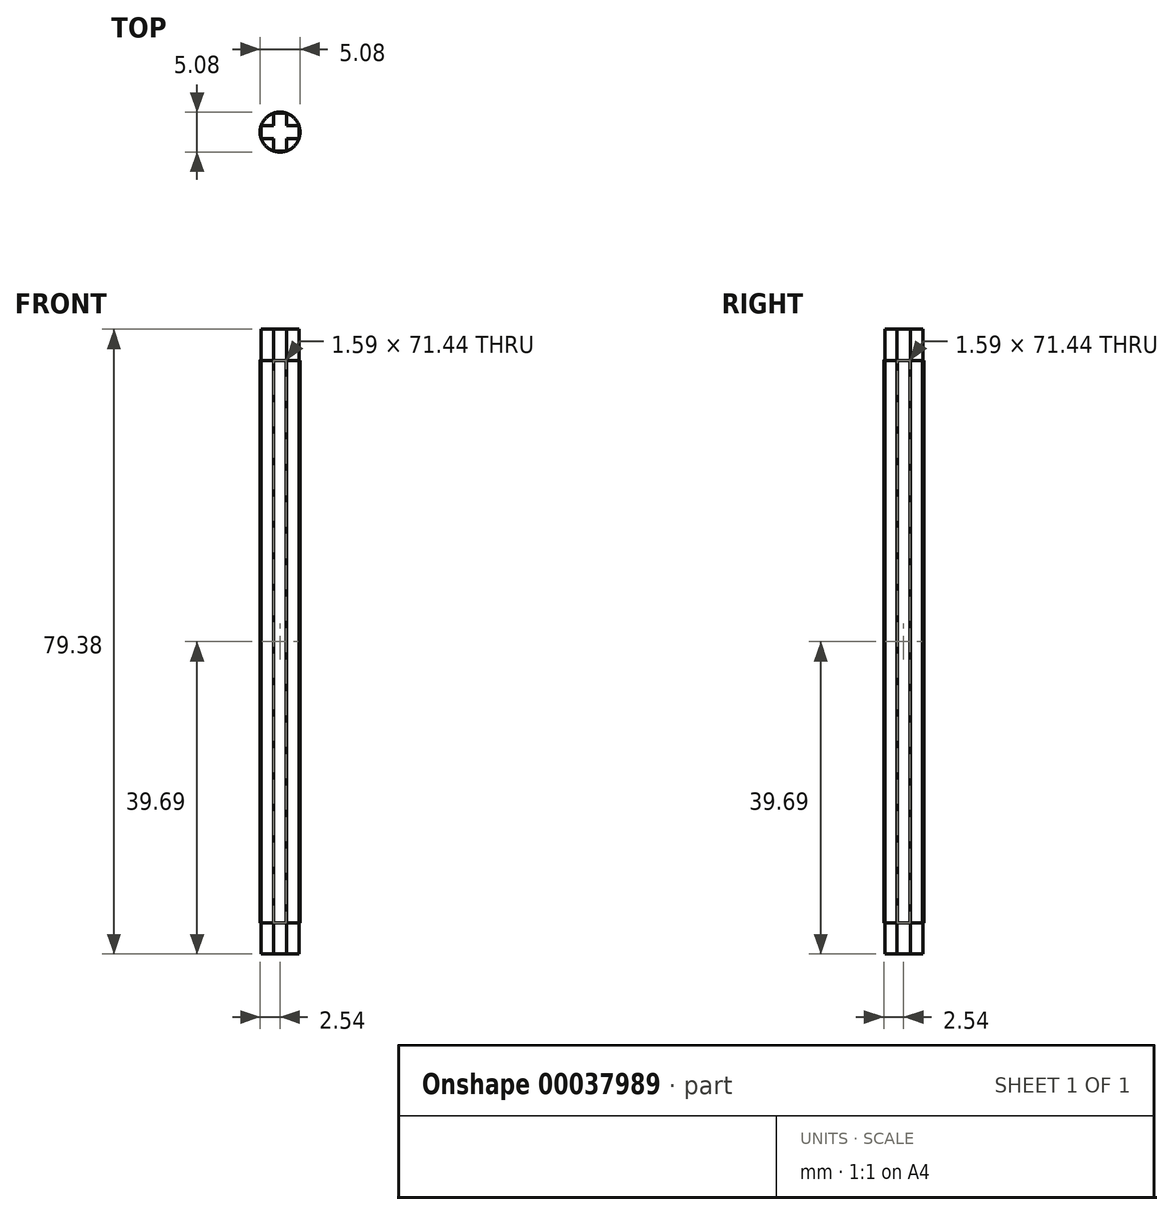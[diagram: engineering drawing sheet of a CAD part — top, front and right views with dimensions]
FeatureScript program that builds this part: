
annotation { "Feature Type Name" : "Feature", "Feature Type Description" : "" }
export const myFeature = defineFeature(function(context is Context, id is Id, definition is map)
    precondition{}
    {
        {
            var Q0;
            Q0=qCreatedBy(makeId("Top.planeOp"),FACE);
            var sketch = newSketch(context, id + "F0", { "sketchPlane" : qUnion([Q0])});
            skLineSegment(sketch, "E0.rect.bottom", {"start": v(0.84, -2.41) * mm, "end": v(-0.84, -2.41) * mm});
            skLineSegment(sketch, "E0.rect.top", {"start": v(0.84, 2.41) * mm, "end": v(-0.84, 2.41) * mm});
            skLineSegment(sketch, "E0.rect.left", {"start": v(0.84, -2.41) * mm, "end": v(0.84, 2.41) * mm});
            skLineSegment(sketch, "E0.rect.right", {"start": v(-0.84, -2.41) * mm, "end": v(-0.84, 2.41) * mm});
            skPoint(sketch, "E0.rect.middle", {"position": v(0, 0) * mm});
            skLineSegment(sketch, "E1.rect.bottom", {"start": v(2.41, -0.84) * mm, "end": v(-2.41, -0.84) * mm});
            skLineSegment(sketch, "E1.rect.top", {"start": v(2.41, 0.84) * mm, "end": v(-2.41, 0.84) * mm});
            skLineSegment(sketch, "E1.rect.left", {"start": v(2.41, -0.84) * mm, "end": v(2.41, 0.84) * mm});
            skLineSegment(sketch, "E1.rect.right", {"start": v(-2.41, -0.84) * mm, "end": v(-2.41, 0.84) * mm});
            skSolve(sketch);
        }
        {
            var Q0;
            Q0 = qSketchRegion(id + "F0", true);
            extrude(context, id + "F1", {"entities" : qUnion([Q0]), "endBound" : BoundingType.SYMMETRIC, "depth" : 79.38 * mm});
        }
        {
            var Q0;
            Q0=qCreatedBy(makeId("Top.planeOp"),FACE);
            var sketch = newSketch(context, id + "F2", { "sketchPlane" : qUnion([Q0])});
            skCircle(sketch, "E2", {"center": v(0, 0) * mm, "radius": 2.54 * mm});
            skSolve(sketch);
        }
        {
            var Q0;
            Q0 = qSketchRegion(id + "F2", true);
            extrude(context, id + "F3", {"entities" : qUnion([Q0]), "operationType" : NewBodyOperationType.ADD, "endBound" : BoundingType.SYMMETRIC, "depth" : 71.44 * mm});
        }
    });
